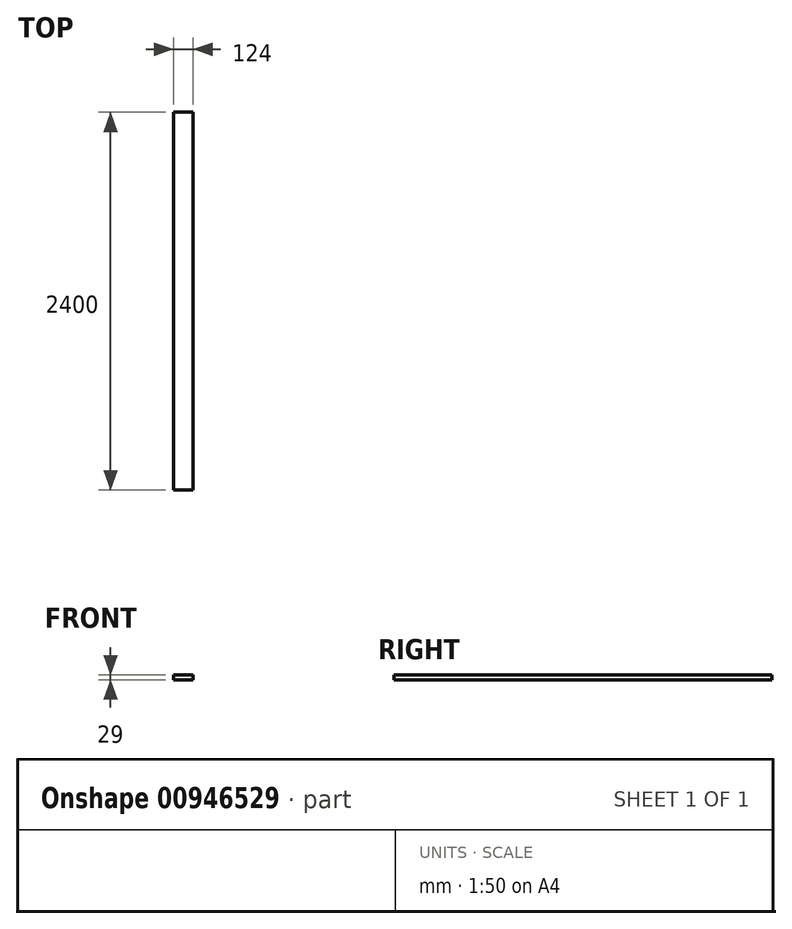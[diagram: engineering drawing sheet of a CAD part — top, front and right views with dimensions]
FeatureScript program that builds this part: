
annotation { "Feature Type Name" : "Feature", "Feature Type Description" : "" }
export const myFeature = defineFeature(function(context is Context, id is Id, definition is map)
    precondition{}
    {
        {
            var Q0;
            Q0=qCreatedBy(makeId("Front.planeOp"),FACE);
            var sketch = newSketch(context, id + "F0", { "sketchPlane" : qUnion([Q0])});
            skLineSegment(sketch, "E0.bottom", {"start": v(0, 0) * mm, "end": v(124, 0) * mm});
            skLineSegment(sketch, "E0.top", {"start": v(0, 29) * mm, "end": v(124, 29) * mm});
            skLineSegment(sketch, "E0.left", {"start": v(0, 0) * mm, "end": v(0, 29) * mm});
            skLineSegment(sketch, "E0.right", {"start": v(124, 0) * mm, "end": v(124, 29) * mm});
            skSolve(sketch);
        }
        {
            var Q0;
            Q0 = qSketchRegion(id + "F0", true);
            extrude(context, id + "F1", {"entities" : qUnion([Q0]), "depth" : 2400 * mm, "offsetDistance" : 25 * mm});
        }
    });
